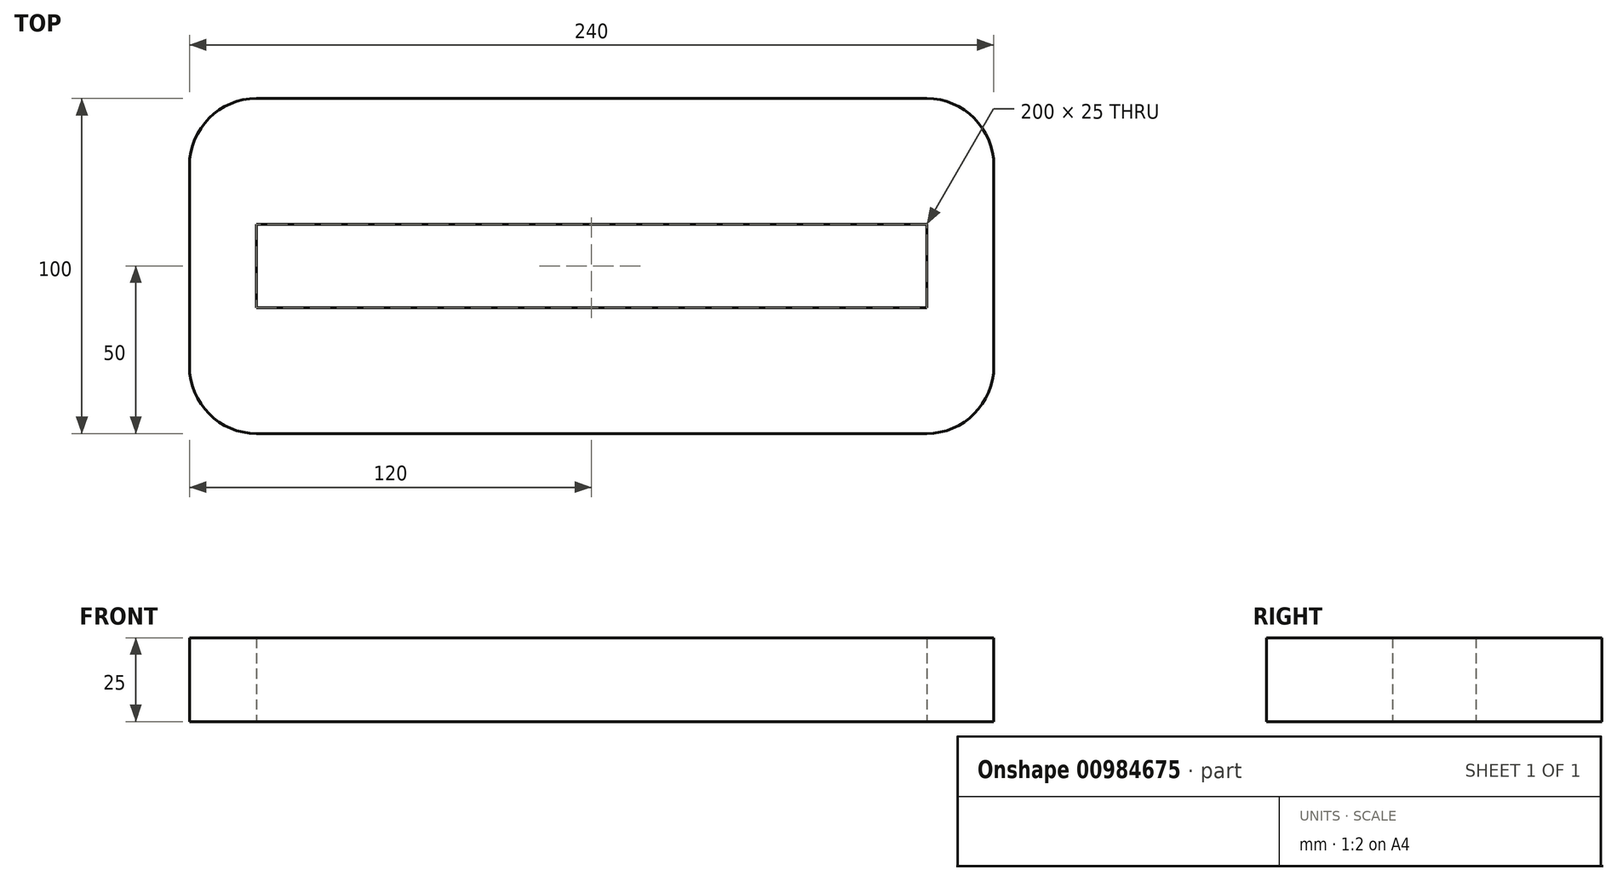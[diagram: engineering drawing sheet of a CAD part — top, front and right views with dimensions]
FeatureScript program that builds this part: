
annotation { "Feature Type Name" : "Feature", "Feature Type Description" : "" }
export const myFeature = defineFeature(function(context is Context, id is Id, definition is map)
    precondition{}
    {
        {
            var Q0;
            Q0=qCreatedBy(makeId("Top.planeOp"),FACE);
            var sketch = newSketch(context, id + "F0", { "sketchPlane" : qUnion([Q0])});
            skLineSegment(sketch, "E0.bottom", {"start": v(120, 50) * mm, "end": v(-120, 50) * mm});
            skLineSegment(sketch, "E0.top", {"start": v(120, -50) * mm, "end": v(-120, -50) * mm});
            skLineSegment(sketch, "E0.left", {"start": v(120, 50) * mm, "end": v(120, -50) * mm});
            skLineSegment(sketch, "E0.right", {"start": v(-120, 50) * mm, "end": v(-120, -50) * mm});
            skLineSegment(sketch, "E1", {"start": v(0, 67.3) * mm, "end": v(0, -64.42) * mm, "construction": true});
            skLineSegment(sketch, "E2", {"start": v(-137.1, 0) * mm, "end": v(137.48, 0) * mm, "construction": true});
            skLineSegment(sketch, "E3.bottom", {"start": v(100, 12.5) * mm, "end": v(-100, 12.5) * mm});
            skLineSegment(sketch, "E3.top", {"start": v(100, -12.5) * mm, "end": v(-100, -12.5) * mm});
            skLineSegment(sketch, "E3.left", {"start": v(100, 12.5) * mm, "end": v(100, -12.5) * mm});
            skLineSegment(sketch, "E3.right", {"start": v(-100, 12.5) * mm, "end": v(-100, -12.5) * mm});
            skPoint(sketch, "E3.middle", {"position": v(0, 0) * mm});
            skSolve(sketch);
        }
        {
            var Q0;
            Q0 = qSketchRegion(id + "F0", true);
            extrude(context, id + "F1", {"entities" : qUnion([Q0]), "depth" : 25 * mm, "offsetDistance" : 25 * mm});
        }
        {
            var Q0;
            Q0=makeQuery(id+"F1.opExtrude","SWEPT_EDGE",EDGE,{"disambiguationData":[OSD([sQuery(id+"F0.wireOp",EDGE,"E0.top"),sQuery(id+"F0.wireOp",EDGE,"E0.right")])]});
            var Q1;
            Q1=makeQuery(id+"F1.opExtrude","SWEPT_EDGE",EDGE,{"disambiguationData":[OSD([sQuery(id+"F0.wireOp",EDGE,"E0.top"),sQuery(id+"F0.wireOp",EDGE,"E0.left")])]});
            var Q2;
            Q2=makeQuery(id+"F1.opExtrude","SWEPT_EDGE",EDGE,{"disambiguationData":[OSD([sQuery(id+"F0.wireOp",EDGE,"E0.bottom"),sQuery(id+"F0.wireOp",EDGE,"E0.left")])]});
            var Q3;
            Q3=makeQuery(id+"F1.opExtrude","SWEPT_EDGE",EDGE,{"disambiguationData":[OSD([sQuery(id+"F0.wireOp",EDGE,"E0.bottom"),sQuery(id+"F0.wireOp",EDGE,"E0.right")])]});
            fillet(context, id + "F2", {"entities" : qUnion([Q0, Q1, Q2, Q3]), "radius" : 20 * mm, "tangentPropagation" : true, "allowEdgeOverflow" : false});
        }
    });
